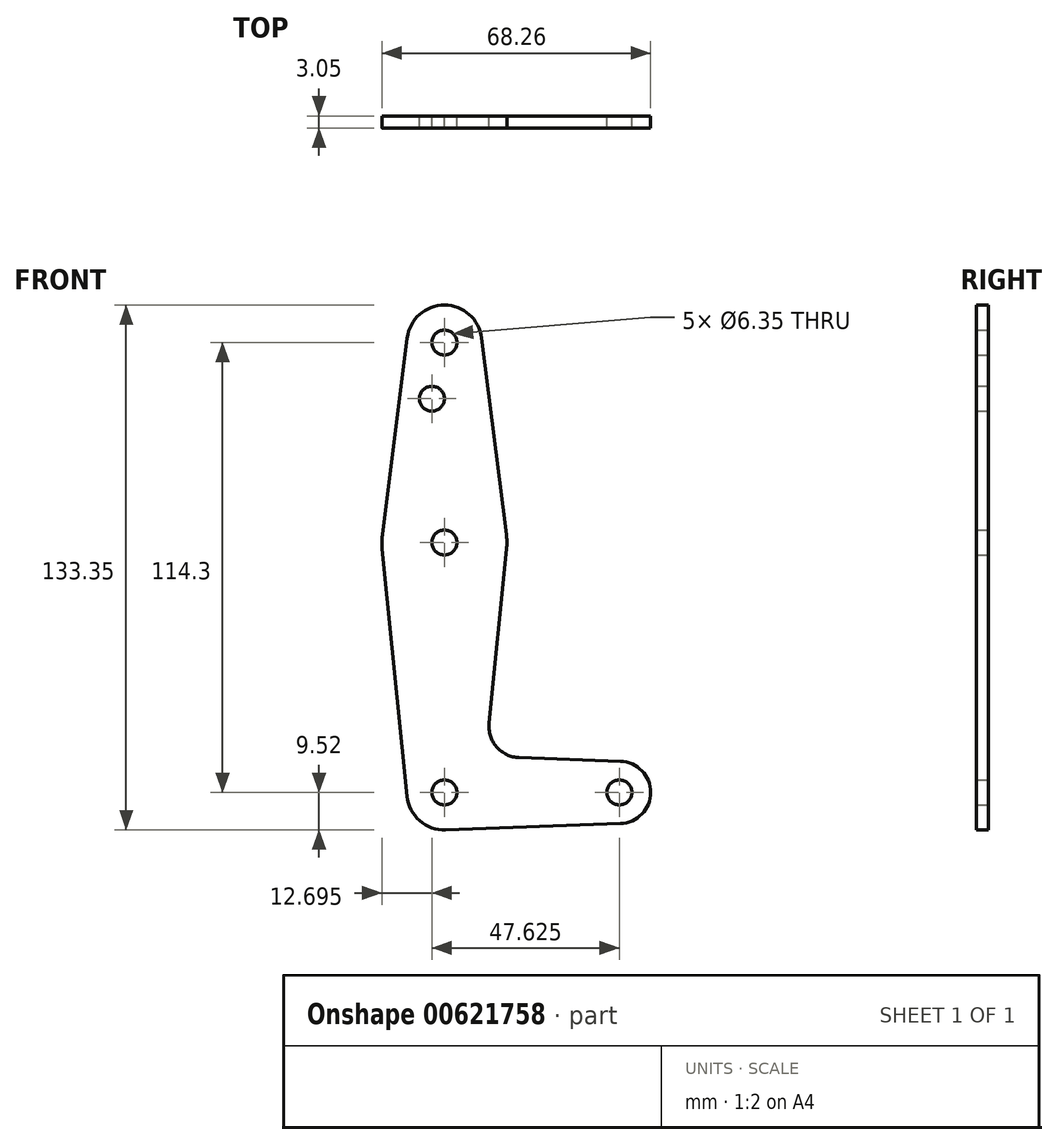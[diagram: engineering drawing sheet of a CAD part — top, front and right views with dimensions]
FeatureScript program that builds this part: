
annotation { "Feature Type Name" : "Feature", "Feature Type Description" : "" }
export const myFeature = defineFeature(function(context is Context, id is Id, definition is map)
    precondition{}
    {
        {
            var Q0;
            Q0=qCreatedBy(makeId("Front.planeOp"),FACE);
            var sketch = newSketch(context, id + "F0", { "sketchPlane" : qUnion([Q0])});
            skLineSegment(sketch, "E0", {"start": v(0, 0) * mm, "end": v(0, 114.3) * mm, "construction": true});
            skLineSegment(sketch, "E1", {"start": v(0, 0) * mm, "end": v(44.45, 0) * mm, "construction": true});
            skCircle(sketch, "E2", {"center": v(0, 0) * mm, "radius": 9.53 * mm});
            skCircle(sketch, "E3", {"center": v(0, 63.5) * mm, "radius": 15.88 * mm});
            skCircle(sketch, "E4", {"center": v(44.45, 0) * mm, "radius": 7.94 * mm});
            skCircle(sketch, "E5", {"center": v(0, 114.3) * mm, "radius": 9.53 * mm});
            skLineSegment(sketch, "E6", {"start": v(-9.45, 115.5) * mm, "end": v(-15.75, 65.48) * mm});
            skLineSegment(sketch, "E7", {"start": v(9.45, 115.5) * mm, "end": v(15.75, 65.48) * mm});
            skLineSegment(sketch, "E8", {"start": v(-15.8, 61.91) * mm, "end": v(-9.48, -0.95) * mm});
            skLineSegment(sketch, "E9", {"start": v(15.8, 61.91) * mm, "end": v(11.34, 17.6) * mm});
            skLineSegment(sketch, "E10", {"start": v(18.97, 8.85) * mm, "end": v(44.73, 7.93) * mm});
            skLineSegment(sketch, "E11", {"start": v(44.73, -7.93) * mm, "end": v(0.34, -9.52) * mm});
            skCircle(sketch, "E12", {"center": v(0, 114.3) * mm, "radius": 3.18 * mm});
            skCircle(sketch, "E13", {"center": v(-3.18, 100.03) * mm, "radius": 3.18 * mm});
            skCircle(sketch, "E14", {"center": v(0, 63.5) * mm, "radius": 3.18 * mm});
            skCircle(sketch, "E15", {"center": v(0, 0) * mm, "radius": 3.18 * mm});
            skCircle(sketch, "E16", {"center": v(44.45, 0) * mm, "radius": 3.18 * mm});
            skArc(sketch, "E17.filletArc", {"start": v(11.34, 17.6) * mm, "mid": v(13.26, 11.57) * mm, "end": v(18.97, 8.85) * mm});
            skLineSegment(sketch, "E18", {"start": v(-3.18, 100.03) * mm, "end": v(0, 100.03) * mm, "construction": true});
            skSolve(sketch);
        }
        {
            var Q0;
            Q0 = qSketchRegion(id + "F0", true);
            extrude(context, id + "F1", {"entities" : qUnion([Q0]), "depth" : 3.05 * mm, "offsetDistance" : 25.4 * mm});
        }
    });
